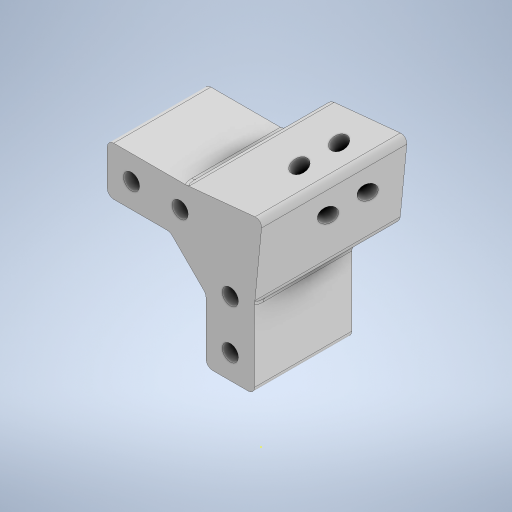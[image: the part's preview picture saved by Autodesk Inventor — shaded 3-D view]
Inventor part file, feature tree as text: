
AUTODESK INVENTOR PART (.ipt)
format: ipt  version: 2024.3 (Build 283343000, 343)  size: 413,696 bytes
history: native  units: mm
features: sketch x13, extrude x9, projected_geometry x6, hole x3, other x1, fillet x1
ambient origin geometry x8: Origin, YZ Plane, XZ Plane, XY Plane, X Axis, Y Axis, Z Axis, Center Point
bodies: Body1 (feature_tree)
feature tree (33):
  other  "ソリッド1"
  extrude  "押し出し1"  Depth=60.0mm
  hole  "穴1"  [1 undecoded]
  extrude  "押し出し2"  Depth=30.0mm TaperAngle=0.0deg
  extrude  "押し出し11"  Depth=7.5mm
  extrude  "押し出し12"  Depth=7.5mm
  extrude  "押し出し17"  Depth=10.5mm
  extrude  "押し出し18"  Depth=10.5mm
  sketch  "スケッチ27"
  extrude  "押し出し19"  Depth=15.0mm
  hole  "穴4"  [1 undecoded]
  hole  "穴5"  [1 undecoded]
  fillet  "フィレット1"  Radius=26.0mm
  extrude  "押し出し20"  Depth=7.5mm
  extrude  "押し出し21"  Depth=7.5mm
  sketch  "スケッチ1"
  sketch  "スケッチ2"
  sketch  "スケッチ3"
  projected_geometry  "投影ループ1"
  sketch  "スケッチ15"
  projected_geometry  "投影ループ10"
  sketch  "スケッチ16"
  projected_geometry  "投影ループ11"
  sketch  "スケッチ25"
  projected_geometry  "投影ループ18"
  sketch  "スケッチ26"
  projected_geometry  "投影ループ19"
  sketch  "スケッチ28"
  sketch  "スケッチ29"
  sketch  "スケッチ30"
  sketch  "スケッチ31"
  projected_geometry  "投影ループ20"
  sketch  "スケッチ32"
note: 3 required parameter values undecoded (feature->parameter linkage not recoverable at this tier; creation-order binding heuristic only, values carry confidence <= 0.55)
